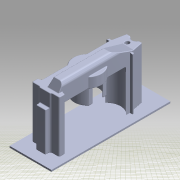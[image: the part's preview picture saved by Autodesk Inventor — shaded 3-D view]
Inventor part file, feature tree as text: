
AUTODESK INVENTOR PART (.ipt)
format: ipt  version: 2018 (Build 220112000, 112)  size: 1,574,400 bytes
history: native  units: mm (DEFAULTED — no unit token found)
features: fillet x11, extrude x9, sketch x9, mirror x5, plane x1, projected_geometry x1, other x1
ambient origin geometry x8: Origin, YZ Plane, XZ Plane, XY Plane, X Axis, Y Axis, Z Axis, Center Point
bodies: Solid1 (feature_tree)
feature tree (37):
  extrude  "Extrusion1"  Depth=100.0mm TaperAngle=0.0deg
  extrude  "Extrusion2"  Depth=100.0mm TaperAngle=0.0deg
  extrude  "Extrusion3"  Depth=0.378mm
  fillet  "Fillet2"  Radius=10.0mm
  plane  "Work Plane1"
  mirror  "Mirror1"
  mirror  "Mirror2"
  extrude  "Extrusion4"  Depth=50.0mm TaperAngle=0.0deg
  extrude  "Extrusion5"  Depth=1.27mm
  extrude  "Extrusion6"  Depth=50.0mm TaperAngle=0.0deg
  mirror  "Mirror3"
  fillet  "Fillet3"  Radius=0.381mm
  extrude  "Extrusion7"  Depth=3.0mm TaperAngle=0.0deg
  mirror  "Mirror4"
  fillet  "Fillet4"  Radius=4.3mm
  fillet  "Fillet5"  Radius=0.3mm
  extrude  "Extrusion8"  Depth=0.3mm
  mirror  "Mirror5"
  fillet  "Fillet6"  Radius=0.3mm
  fillet  "Fillet7"  Radius=0.3mm
  fillet  "Fillet8"  Radius=0.2mm
  fillet  "Fillet9"  Radius=1.0mm
  fillet  "Fillet10"  [1 undecoded]
  fillet  "Fillet11"  [1 undecoded]
  fillet  "Fillet12"  [1 undecoded]
  extrude  "Extrusion9"  [1 undecoded]
  sketch  "Sketch1"  dims[d0=0.1mm d3=100.0mm d4=0.0mm]
  sketch  "Sketch2"  dims[d5=0.1mm d6=100.0mm d7=0.0mm]
  sketch  "Sketch3"  dims[d8=2.0mm d9=0.0mm d11=0.378mm d12=10.0mm d13=0.0mm]
  projected_geometry  "Projected Loop2"
  sketch  "Sketch4"  dims[d14=5.08mm d15=50.0mm d16=0.0mm]
  sketch  "Sketch5"  dims[d17=50.0mm d18=0.0mm d19=1.27mm]
  sketch  "Sketch6"  dims[d20=1.0mm d22=50.0mm d23=0.0mm d24=0.381mm]
  sketch  "Sketch7"  dims[d25=2.78mm d26=3.0mm d27=0.0mm d28=4.3mm d29=0.3mm]
  sketch  "Sketch8"  dims[d30=0.3mm d31=0.3mm d32=0.3mm d33=0.3mm d34=0.2mm d35=1.0mm d36=0.0mm]
  sketch  "Sketch9"
  other  "Body-Move_Copy1"
note: 4 required parameter values undecoded (feature->parameter linkage not recoverable at this tier; creation-order binding heuristic only, values carry confidence <= 0.55)
